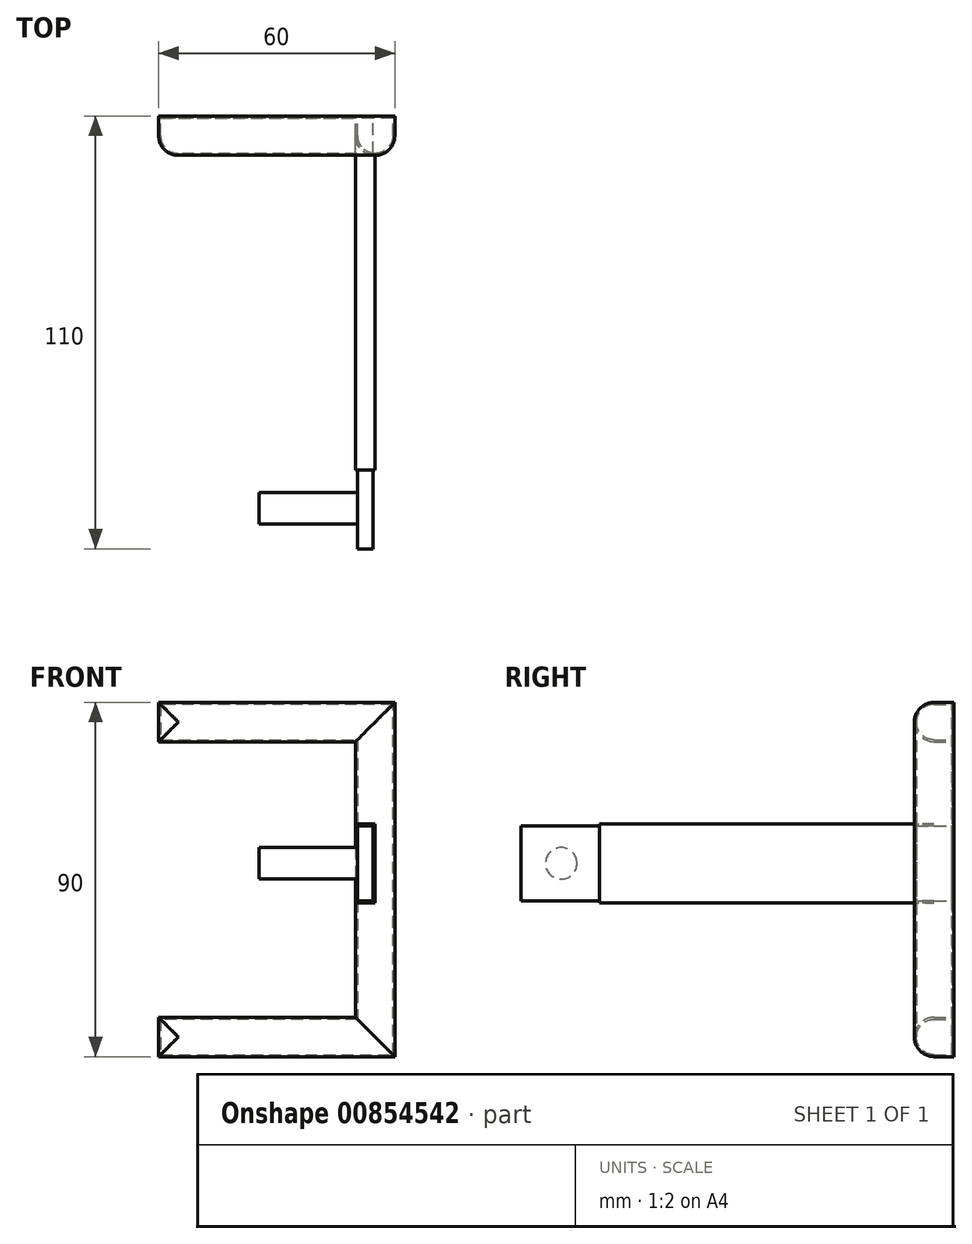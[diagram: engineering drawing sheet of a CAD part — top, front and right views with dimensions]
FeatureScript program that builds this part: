
annotation { "Feature Type Name" : "Feature", "Feature Type Description" : "" }
export const myFeature = defineFeature(function(context is Context, id is Id, definition is map)
    precondition{}
    {
        {
            var Q0;
            Q0=qCreatedBy(makeId("Front.planeOp"),FACE);
            var sketch = newSketch(context, id + "F0", { "sketchPlane" : qUnion([Q0])});
            skLineSegment(sketch, "E0", {"start": v(-10, 30.88) * mm, "end": v(40, 30.88) * mm});
            skLineSegment(sketch, "E1", {"start": v(40, 30.88) * mm, "end": v(40, -39.12) * mm});
            skLineSegment(sketch, "E2", {"start": v(40, -39.12) * mm, "end": v(-10, -39.12) * mm});
            skLineSegment(sketch, "E3", {"start": v(-10, -39.12) * mm, "end": v(-10, -49.12) * mm});
            skLineSegment(sketch, "E4", {"start": v(-10, -49.12) * mm, "end": v(50, -49.12) * mm});
            skLineSegment(sketch, "E5", {"start": v(50, -49.12) * mm, "end": v(50, 40.88) * mm});
            skLineSegment(sketch, "E6", {"start": v(50, 40.88) * mm, "end": v(-10, 40.88) * mm});
            skLineSegment(sketch, "E7", {"start": v(-10, 40.88) * mm, "end": v(-10, 30.88) * mm});
            skSolve(sketch);
        }
        {
            var Q0;
            Q0=makeQuery(id+"F0.imprint","IMPRINT",FACE,{"disambiguationData":[TD([[makeQuery(id+"F0.imprint","IMPRINT",EDGE,{"derivedFrom":sQuery(id+"F0.wireOp",EDGE,"E0")}),1.0]])]});
            extrude(context, id + "F1", {"entities" : qUnion([Q0]), "depth" : 10 * mm, "offsetDistance" : 25 * mm});
        }
        {
            var Q0;
            Q0=makeQuery(id+"F1.opExtrude","CAP_FACE",FACE,{"disambiguationData":[OSD([sQuery(id+"F0.wireOp",EDGE,"E0"),sQuery(id+"F0.wireOp",EDGE,"E1"),sQuery(id+"F0.wireOp",EDGE,"E2"),sQuery(id+"F0.wireOp",EDGE,"E3"),sQuery(id+"F0.wireOp",EDGE,"E4"),sQuery(id+"F0.wireOp",EDGE,"E5"),sQuery(id+"F0.wireOp",EDGE,"E6"),sQuery(id+"F0.wireOp",EDGE,"E7")])],"isStart":false});
            fillet(context, id + "F2", {"entities" : qUnion([Q0]), "radius" : 5 * mm, "tangentPropagation" : true, "allowEdgeOverflow" : false});
        }
        {
            var Q0;
            Q0=qCreatedBy(makeId("Front.planeOp"),FACE);
            var sketch = newSketch(context, id + "F3", { "sketchPlane" : qUnion([Q0])});
            skLineSegment(sketch, "E8.bottom", {"start": v(40, 10) * mm, "end": v(45, 10) * mm});
            skLineSegment(sketch, "E8.top", {"start": v(40, -10) * mm, "end": v(45, -10) * mm});
            skLineSegment(sketch, "E8.left", {"start": v(40, 10) * mm, "end": v(40, -10) * mm});
            skLineSegment(sketch, "E8.right", {"start": v(45, 10) * mm, "end": v(45, -10) * mm});
            skSolve(sketch);
        }
        {
            var Q0;
            Q0 = qSketchRegion(id + "F3", true);
            extrude(context, id + "F4", {"entities" : qUnion([Q0]), "operationType" : NewBodyOperationType.ADD, "depth" : 90 * mm, "offsetDistance" : 25 * mm});
        }
        {
            var Q0;
            Q0=makeQuery(id+"F4.opExtrude","CAP_FACE",FACE,{"disambiguationData":[OSD([sQuery(id+"F3.wireOp",EDGE,"E8.bottom"),sQuery(id+"F3.wireOp",EDGE,"E8.top"),sQuery(id+"F3.wireOp",EDGE,"E8.left"),sQuery(id+"F3.wireOp",EDGE,"E8.right")])],"isStart":false});
            shell(context, id + "F5", {"entities" : qUnion([Q0]), "thickness" : 0.5 * mm});
        }
        {
            var Q0;
            Q0=qCreatedBy(makeId("Front.planeOp"),FACE);
            var sketch = newSketch(context, id + "F6", { "sketchPlane" : qUnion([Q0])});
            skLineSegment(sketch, "E9.bottom", {"start": v(40.5, 9.5) * mm, "end": v(44.5, 9.5) * mm});
            skLineSegment(sketch, "E9.top", {"start": v(40.5, -9.5) * mm, "end": v(44.5, -9.5) * mm});
            skLineSegment(sketch, "E9.left", {"start": v(40.5, 9.5) * mm, "end": v(40.5, -9.5) * mm});
            skLineSegment(sketch, "E9.right", {"start": v(44.5, 9.5) * mm, "end": v(44.5, -9.5) * mm});
            skSolve(sketch);
        }
        {
            var Q0;
            Q0 = qSketchRegion(id + "F6", true);
            extrude(context, id + "F7", {"entities" : qUnion([Q0]), "operationType" : NewBodyOperationType.ADD, "depth" : 110 * mm, "offsetDistance" : 25 * mm});
        }
        {
            var Q0;
            Q0=makeQuery(id+"F7.opExtrude","SWEPT_FACE",FACE,{"disambiguationData":[OSD([sQuery(id+"F6.wireOp",EDGE,"E9.left")])]});
            var sketch = newSketch(context, id + "F8", { "sketchPlane" : qUnion([Q0])});
            skCircle(sketch, "E10", {"center": v(99.72, 0) * mm, "radius": 4 * mm});
            skSolve(sketch);
        }
        {
            var Q0;
            Q0=makeQuery(id+"F8.imprint","IMPRINT",FACE,{"disambiguationData":[TD([[makeQuery(id+"F8.imprint","IMPRINT",EDGE,{"derivedFrom":sQuery(id+"F8.wireOp",EDGE,"E10")}),1.0]])]});
            extrude(context, id + "F9", {"entities" : qUnion([Q0]), "depth" : 25 * mm, "offsetDistance" : 25 * mm});
        }
    });
